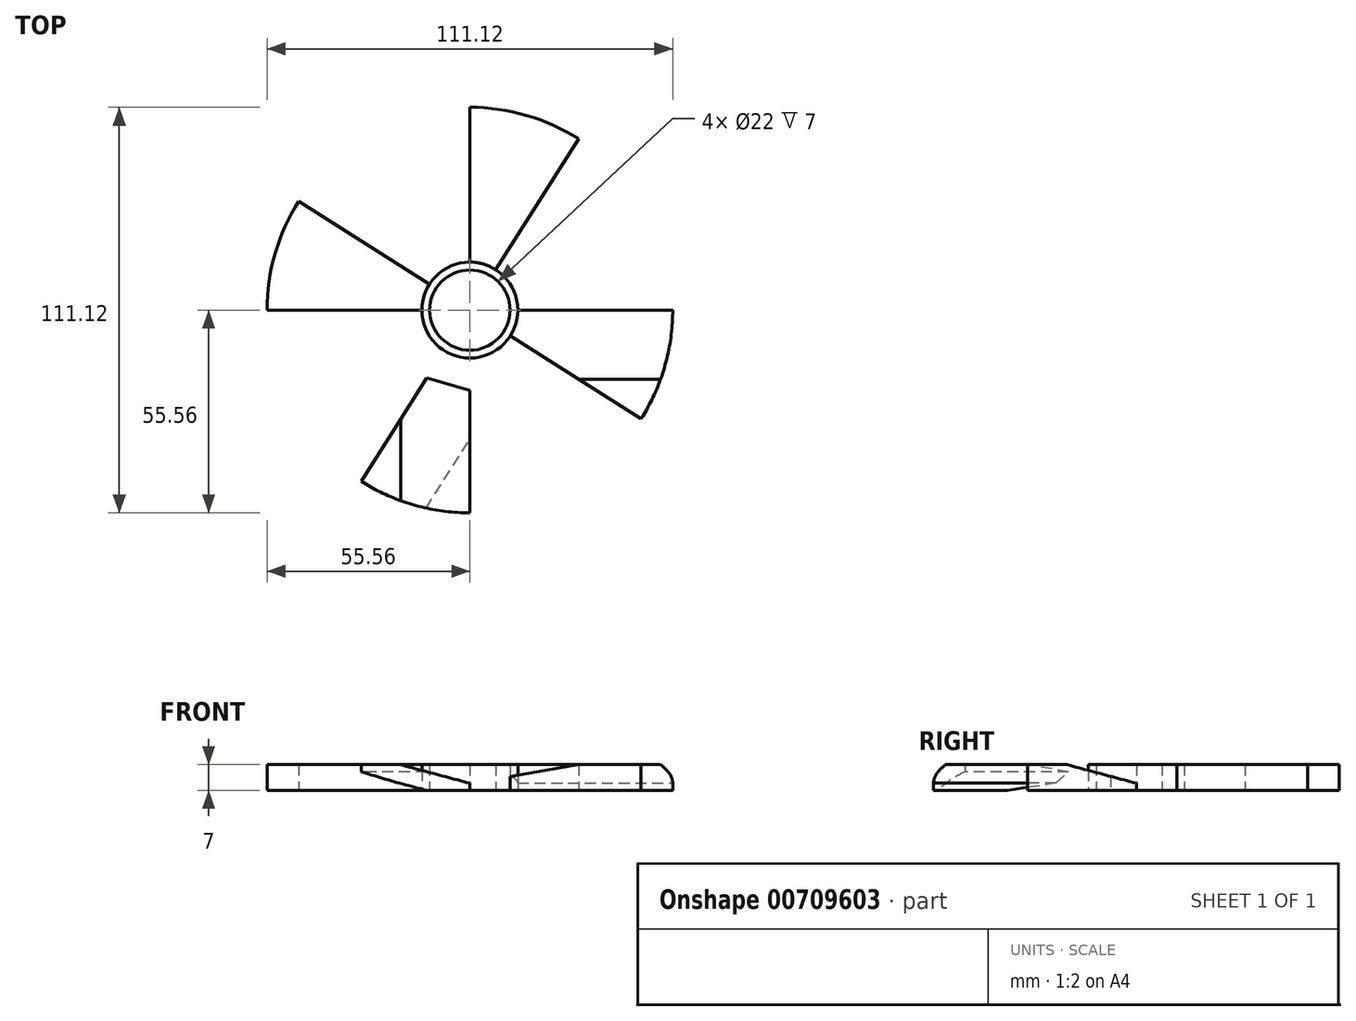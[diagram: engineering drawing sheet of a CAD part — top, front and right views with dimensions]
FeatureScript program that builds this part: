
annotation { "Feature Type Name" : "Feature", "Feature Type Description" : "" }
export const myFeature = defineFeature(function(context is Context, id is Id, definition is map)
    precondition{}
    {
        {
            var Q0;
            Q0=qCreatedBy(makeId("Top.planeOp"),FACE);
            var sketch = newSketch(context, id + "F0", { "sketchPlane" : qUnion([Q0])});
            skCircle(sketch, "E0", {"center": v(0, 0) * mm, "radius": 11 * mm});
            skLineSegment(sketch, "E1", {"start": v(0, 0) * mm, "end": v(0, 53.34) * mm});
            skLineSegment(sketch, "E2", {"start": v(0, 0) * mm, "end": v(53.34, 0) * mm});
            skLineSegment(sketch, "E3", {"start": v(0, 0) * mm, "end": v(-53.34, 0) * mm});
            skLineSegment(sketch, "E4", {"start": v(0, 0) * mm, "end": v(0, -53.34) * mm});
            skCircle(sketch, "E5", {"center": v(0, 0) * mm, "radius": 55.56 * mm});
            skLineSegment(sketch, "E6", {"start": v(0, 0) * mm, "end": v(-29.8, -46.9) * mm});
            skLineSegment(sketch, "E7", {"start": v(0, 0) * mm, "end": v(-46.9, 29.8) * mm});
            skLineSegment(sketch, "E8", {"start": v(0, 0) * mm, "end": v(29.8, 46.9) * mm});
            skLineSegment(sketch, "E9", {"start": v(0, 0) * mm, "end": v(46.9, -29.8) * mm});
            skLineSegment(sketch, "E10", {"start": v(-29.8, -46.9) * mm, "end": v(0, -53.34) * mm});
            skLineSegment(sketch, "E11", {"start": v(-46.9, 29.8) * mm, "end": v(-53.34, 0) * mm});
            skLineSegment(sketch, "E12", {"start": v(0, 53.34) * mm, "end": v(29.8, 46.9) * mm});
            skLineSegment(sketch, "E13", {"start": v(53.34, 0) * mm, "end": v(46.9, -29.8) * mm});
            skLineSegment(sketch, "E14", {"start": v(0, 0) * mm, "end": v(0, 55.56) * mm});
            skLineSegment(sketch, "E15", {"start": v(0, 55.56) * mm, "end": v(0, 0) * mm});
            skLineSegment(sketch, "E16", {"start": v(-55.56, 0) * mm, "end": v(0, 0) * mm});
            skLineSegment(sketch, "E17", {"start": v(0, 0) * mm, "end": v(0, -55.56) * mm});
            skLineSegment(sketch, "E18", {"start": v(0, 0) * mm, "end": v(55.56, 0) * mm});
            skCircle(sketch, "E19", {"center": v(0, 0) * mm, "radius": 13.14 * mm});
            skSolve(sketch);
        }
        {
            var Q0;
            {var subQ0=sQuery(id+"F0.wireOp",EDGE,"E7");var subQ1=sQuery(id+"F0.wireOp",EDGE,"E0");var subQ2=makeQuery(id+"F0.imprint","INTERSECT",VERTEX,{"derivedFrom":[subQ1,subQ0]});Q0=makeQuery(id+"F0.imprint","IMPRINT",FACE,{"disambiguationData":[TD([[makeQuery(id+"F0.imprint","IMPRINT",EDGE,{"disambiguationData":[TD([[subQ2,-1.0]])],"derivedFrom":subQ1}),-1.0]])]});}
            var Q1;
            {var subQ0=sQuery(id+"F0.wireOp",EDGE,"E15");var subQ1=sQuery(id+"F0.wireOp",EDGE,"E0");var subQ2=makeQuery(id+"F0.imprint","INTERSECT",VERTEX,{"derivedFrom":[subQ1,subQ0]});Q1=makeQuery(id+"F0.imprint","IMPRINT",FACE,{"disambiguationData":[TD([[makeQuery(id+"F0.imprint","IMPRINT",EDGE,{"disambiguationData":[TD([[subQ2,-1.0]])],"derivedFrom":subQ1}),-1.0]])]});}
            var Q2;
            {var subQ0=sQuery(id+"F0.wireOp",EDGE,"E8");var subQ1=sQuery(id+"F0.wireOp",EDGE,"E0");var subQ2=makeQuery(id+"F0.imprint","INTERSECT",VERTEX,{"derivedFrom":[subQ1,subQ0]});Q2=makeQuery(id+"F0.imprint","IMPRINT",FACE,{"disambiguationData":[TD([[makeQuery(id+"F0.imprint","IMPRINT",EDGE,{"disambiguationData":[TD([[subQ2,-1.0]])],"derivedFrom":subQ1}),-1.0]])]});}
            var Q3;
            {var subQ0=sQuery(id+"F0.wireOp",EDGE,"E8");var subQ1=sQuery(id+"F0.wireOp",EDGE,"E0");var subQ2=makeQuery(id+"F0.imprint","INTERSECT",VERTEX,{"derivedFrom":[subQ1,subQ0]});Q3=makeQuery(id+"F0.imprint","IMPRINT",FACE,{"disambiguationData":[TD([[makeQuery(id+"F0.imprint","IMPRINT",EDGE,{"disambiguationData":[TD([[subQ2,1.0]])],"derivedFrom":subQ1}),-1.0]])]});}
            var Q4;
            {var subQ0=sQuery(id+"F0.wireOp",EDGE,"E18");var subQ1=sQuery(id+"F0.wireOp",EDGE,"E0");var subQ2=makeQuery(id+"F0.imprint","INTERSECT",VERTEX,{"derivedFrom":[subQ1,subQ0]});Q4=makeQuery(id+"F0.imprint","IMPRINT",FACE,{"disambiguationData":[TD([[makeQuery(id+"F0.imprint","IMPRINT",EDGE,{"disambiguationData":[TD([[subQ2,1.0]])],"derivedFrom":subQ1}),-1.0]])]});}
            var Q5;
            {var subQ0=sQuery(id+"F0.wireOp",EDGE,"E17");var subQ1=sQuery(id+"F0.wireOp",EDGE,"E0");var subQ2=makeQuery(id+"F0.imprint","INTERSECT",VERTEX,{"derivedFrom":[subQ1,subQ0]});Q5=makeQuery(id+"F0.imprint","IMPRINT",FACE,{"disambiguationData":[TD([[makeQuery(id+"F0.imprint","IMPRINT",EDGE,{"disambiguationData":[TD([[subQ2,-1.0]])],"derivedFrom":subQ1}),-1.0]])]});}
            var Q6;
            {var subQ0=sQuery(id+"F0.wireOp",EDGE,"E6");var subQ1=sQuery(id+"F0.wireOp",EDGE,"E0");var subQ2=makeQuery(id+"F0.imprint","INTERSECT",VERTEX,{"derivedFrom":[subQ1,subQ0]});Q6=makeQuery(id+"F0.imprint","IMPRINT",FACE,{"disambiguationData":[TD([[makeQuery(id+"F0.imprint","IMPRINT",EDGE,{"disambiguationData":[TD([[subQ2,-1.0]])],"derivedFrom":subQ1}),-1.0]])]});}
            var Q7;
            {var subQ0=sQuery(id+"F0.wireOp",EDGE,"E16");var subQ1=sQuery(id+"F0.wireOp",EDGE,"E0");var subQ2=makeQuery(id+"F0.imprint","INTERSECT",VERTEX,{"derivedFrom":[subQ1,subQ0]});Q7=makeQuery(id+"F0.imprint","IMPRINT",FACE,{"disambiguationData":[TD([[makeQuery(id+"F0.imprint","IMPRINT",EDGE,{"disambiguationData":[TD([[subQ2,-1.0]])],"derivedFrom":subQ1}),-1.0]])]});}
            extrude(context, id + "F1", {"entities" : qUnion([Q0, Q1, Q2, Q3, Q4, Q5, Q6, Q7]), "depth" : 7 * mm, "offsetDistance" : 25.4 * mm});
        }
        {
            var Q0;
            {var subQ0=sQuery(id+"F0.wireOp",EDGE,"E12");Q0=makeQuery(id+"F0.imprint","IMPRINT",FACE,{"disambiguationData":[TD([[makeQuery(id+"F0.imprint","IMPRINT",EDGE,{"derivedFrom":subQ0}),-1.0]])]});}
            var Q1;
            {var subQ0=sQuery(id+"F0.wireOp",EDGE,"E11");Q1=makeQuery(id+"F0.imprint","IMPRINT",FACE,{"disambiguationData":[TD([[makeQuery(id+"F0.imprint","IMPRINT",EDGE,{"derivedFrom":subQ0}),1.0]])]});}
            var Q2;
            {var subQ0=sQuery(id+"F0.wireOp",EDGE,"E10");Q2=makeQuery(id+"F0.imprint","IMPRINT",FACE,{"disambiguationData":[TD([[makeQuery(id+"F0.imprint","IMPRINT",EDGE,{"derivedFrom":subQ0}),1.0]])]});}
            var Q3;
            {var subQ0=sQuery(id+"F0.wireOp",EDGE,"E13");Q3=makeQuery(id+"F0.imprint","IMPRINT",FACE,{"disambiguationData":[TD([[makeQuery(id+"F0.imprint","IMPRINT",EDGE,{"derivedFrom":subQ0}),-1.0]])]});}
            var Q4;
            {var subQ0=sQuery(id+"F0.wireOp",EDGE,"E12");Q4=makeQuery(id+"F0.imprint","IMPRINT",FACE,{"disambiguationData":[TD([[makeQuery(id+"F0.imprint","IMPRINT",EDGE,{"derivedFrom":subQ0}),1.0]])]});}
            var Q5;
            {var subQ0=sQuery(id+"F0.wireOp",EDGE,"E11");Q5=makeQuery(id+"F0.imprint","IMPRINT",FACE,{"disambiguationData":[TD([[makeQuery(id+"F0.imprint","IMPRINT",EDGE,{"derivedFrom":subQ0}),-1.0]])]});}
            var Q6;
            {var subQ0=sQuery(id+"F0.wireOp",EDGE,"E10");Q6=makeQuery(id+"F0.imprint","IMPRINT",FACE,{"disambiguationData":[TD([[makeQuery(id+"F0.imprint","IMPRINT",EDGE,{"derivedFrom":subQ0}),-1.0]])]});}
            var Q7;
            {var subQ0=sQuery(id+"F0.wireOp",EDGE,"E13");Q7=makeQuery(id+"F0.imprint","IMPRINT",FACE,{"disambiguationData":[TD([[makeQuery(id+"F0.imprint","IMPRINT",EDGE,{"derivedFrom":subQ0}),1.0]])]});}
            extrude(context, id + "F2", {"entities" : qUnion([Q0, Q1, Q2, Q3, Q4, Q5, Q6, Q7]), "depth" : 7 * mm, "offsetDistance" : 25.4 * mm});
        }
        {
            var Q0;
            Q0=makeQuery(id+"F2.opExtrude","CAP_EDGE",EDGE,{"disambiguationData":[OSD([sQuery(id+"F0.wireOp",EDGE,"E17")])],"isStart":false});
            var Q1;
            Q1=makeQuery(id+"F2.opExtrude","CAP_EDGE",EDGE,{"disambiguationData":[OSD([sQuery(id+"F0.wireOp",EDGE,"E18")])],"isStart":false});
            chamfer(context, id + "F3", {"entities" : qUnion([Q0, Q1]), "chamferType" : ChamferType.OFFSET_ANGLE, "width" : 5.08 * mm, "oppositeDirection" : false, "angle" : 75 * degree});
        }
        {
            var Q0;
            Q0=makeQuery(id+"F2.opExtrude","CAP_EDGE",EDGE,{"disambiguationData":[OSD([sQuery(id+"F0.wireOp",EDGE,"E6")])],"isStart":true});
            chamfer(context, id + "F4", {"entities" : qUnion([Q0]), "chamferType" : ChamferType.OFFSET_ANGLE, "width" : 5.08 * mm, "oppositeDirection" : false, "angle" : 75 * degree, "tangentPropagation" : true});
        }
    });
